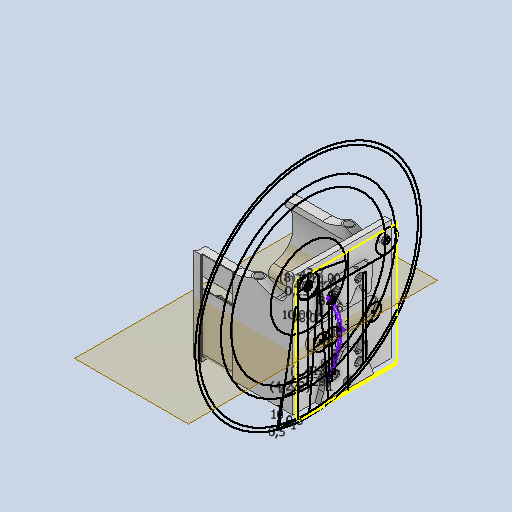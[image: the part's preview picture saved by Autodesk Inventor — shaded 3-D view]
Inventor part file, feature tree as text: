
AUTODESK INVENTOR PART (.ipt)
format: ipt  version: 2022 (Build 260153000, 153)  size: 1,074,688 bytes
history: native  units: mm
features: sketch x22, reference x21, extrude x20, projected_geometry x20, fillet x13, other x9, chamfer x2
ambient origin geometry x8: Origin, YZ Plane, XZ Plane, XY Plane, X Axis, Y Axis, Z Axis, Center Point
bodies: Body1 (feature_tree)
feature tree (107):
  other  "Твердое тело1"
  extrude  "Выдавливание1"  Depth=34.5mm TaperAngle=0.0deg
  extrude  "Выдавливание2"  Depth=0.5mm
  extrude  "Выдавливание3"  Depth=0.3mm
  extrude  "Выдавливание4"  Depth=5.0mm
  extrude  "Выдавливание5"  Depth=5.0mm
  extrude  "Выдавливание6"  Depth=5.0mm
  extrude  "Выдавливание8"  Depth=15.0mm
  extrude  "Выдавливание9"  Depth=15.0mm
  chamfer  "Фаска1"  Distance=15.0mm
  fillet  "Сопряжение1"  Radius=1.7mm
  extrude  "Выдавливание10"  Depth=2.0mm TaperAngle=0.0deg
  extrude  "Выдавливание11"  Depth=0.8mm
  fillet  "Сопряжение2"  Radius=4.7mm
  fillet  "Сопряжение3"  Radius=0.4mm
  fillet  "Сопряжение4"  Radius=0.4mm
  fillet  "Сопряжение5"  Radius=200.0mm
  sketch  "Эскиз15"
  extrude  "Выдавливание12"  Depth=0.5mm TaperAngle=0.0deg
  sketch  "Эскиз17"
  extrude  "Выдавливание13"  Depth=2.3mm TaperAngle=0.0deg
  fillet  "Сопряжение6"  Radius=10.0mm
  fillet  "Сопряжение7"  Radius=10.0mm
  fillet  "Сопряжение8"  Radius=3.0mm
  fillet  "Сопряжение9"  Radius=4.0mm
  extrude  "Выдавливание14"  Depth=3.0mm
  fillet  "Сопряжение10"  Radius=4.0mm
  extrude  "Выдавливание15"  Depth=2.3mm TaperAngle=0.0deg
  extrude  "Выдавливание16"  Depth=2.3mm TaperAngle=45.0deg
  extrude  "Выдавливание17"  Depth=10.0mm
  fillet  "Сопряжение11"  Radius=45.0mm
  fillet  "Сопряжение12"  Radius=30.0mm
  extrude  "Выдавливание18"  Depth=0.8mm TaperAngle=0.0deg
  extrude  "Выдавливание19"  Depth=2.0mm
  extrude  "Выдавливание20"  Depth=1.5mm
  chamfer  "Фаска2"  Distance=0.15mm
  other  "РабПлоскость1"
  extrude  "Выдавливание21"  Depth=3.0mm
  fillet  "Сопряжение16"  Radius=50.0mm
  sketch  "Эскиз1"
  reference  "Ссылка1"
  reference  "Ссылка2"
  reference  "Ссылка3"
  reference  "Ссылка4"
  reference  "Ссылка5"
  reference  "Ссылка6"
  reference  "Ссылка7"
  reference  "Ссылка8"
  sketch  "Эскиз2"
  projected_geometry  "Спроецированная петля1"
  projected_geometry  "Спроецированная петля2"
  sketch  "Эскиз3"
  reference  "Ссылка9"
  reference  "Ссылка10"
  sketch  "Эскиз4"
  projected_geometry  "Спроецированная петля3"
  reference  "Ссылка11"
  reference  "Ссылка12"
  reference  "Ссылка13"
  reference  "Ссылка14"
  sketch  "Эскиз5"
  reference  "Ссылка15"
  reference  "Ссылка16"
  projected_geometry  "Спроецированная петля4"
  sketch  "Эскиз7"
  projected_geometry  "Спроецированная петля6"
  sketch  "Эскиз11"
  projected_geometry  "Спроецированная петля8"
  sketch  "Эскиз12"
  reference  "Ссылка27"
  sketch  "Эскиз13"
  reference  "Ссылка28"
  projected_geometry  "Спроецированная петля9"
  sketch  "Эскиз14"
  sketch  "Эскиз16"
  reference  "Ссылка29"
  projected_geometry  "Спроецированная петля10"
  projected_geometry  "Спроецированная петля11"
  projected_geometry  "Спроецированная петля12"
  reference  "Ссылка30"
  reference  "Ссылка31"
  sketch  "Эскиз18"
  projected_geometry  "Спроецированная петля14"
  sketch  "Эскиз19"
  projected_geometry  "Спроецированная петля15"
  projected_geometry  "Спроецированная петля16"
  sketch  "Эскиз20"
  projected_geometry  "Спроецированная петля17"
  projected_geometry  "Спроецированная петля18"
  sketch  "Эскиз21"
  projected_geometry  "Спроецированная петля19"
  projected_geometry  "Спроецированная петля20"
  projected_geometry  "Спроецированная петля21"
  projected_geometry  "Спроецированная петля22"
  sketch  "Эскиз22"
  sketch  "Эскиз23"
  sketch  "Эскиз24"
  projected_geometry  "Спроецированная петля24"
  sketch  "Эскиз25"
  sketch  "Эскиз26"
  other  "<userpath>\Documents\Git\MZCAT_battery\FastBattery.iam"
  other  "FastBattery.iam"
  other  "plan:1"
  other  "BMS_board:1"
  other  "metal_body_fixed:1"
  other  "ButerBoard:1"
  other  "metal_cap:1"
